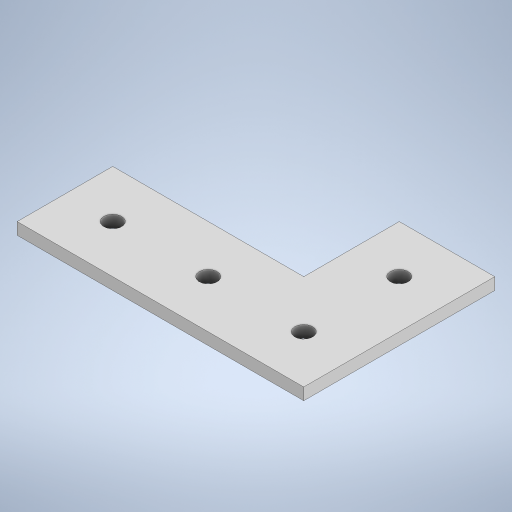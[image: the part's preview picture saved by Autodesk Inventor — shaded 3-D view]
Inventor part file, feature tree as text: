
AUTODESK INVENTOR PART (.ipt)
format: ipt  version: 2023.1 (Build 271208000, 208)  size: 237,568 bytes
history: native  units: in
note: dims shown in document units (in); Inventor stores cm internally (conversion verified against a paired STEP export)
features: extrude x1, sketch x1
ambient origin geometry x8: Origin, YZ Plane, XZ Plane, XY Plane, X Axis, Y Axis, Z Axis, Center Point
bodies: Solid1 (feature_tree)
feature tree (2):
  extrude  "Extrusion1"  Depth=1.0in
  sketch  "Sketch1"  dims[d9=3.0in d10=1.0in d11=2.0in d12=1.0in d13=1.0in d14=2.0in d15=0.5in d16=0.5in d17=0.1875in d18=1.0in d19=0.1875in d20=1.0in d21=0.1875in d22=1.0in d23=0.1875in d24=0.125in d25=0.0in]
